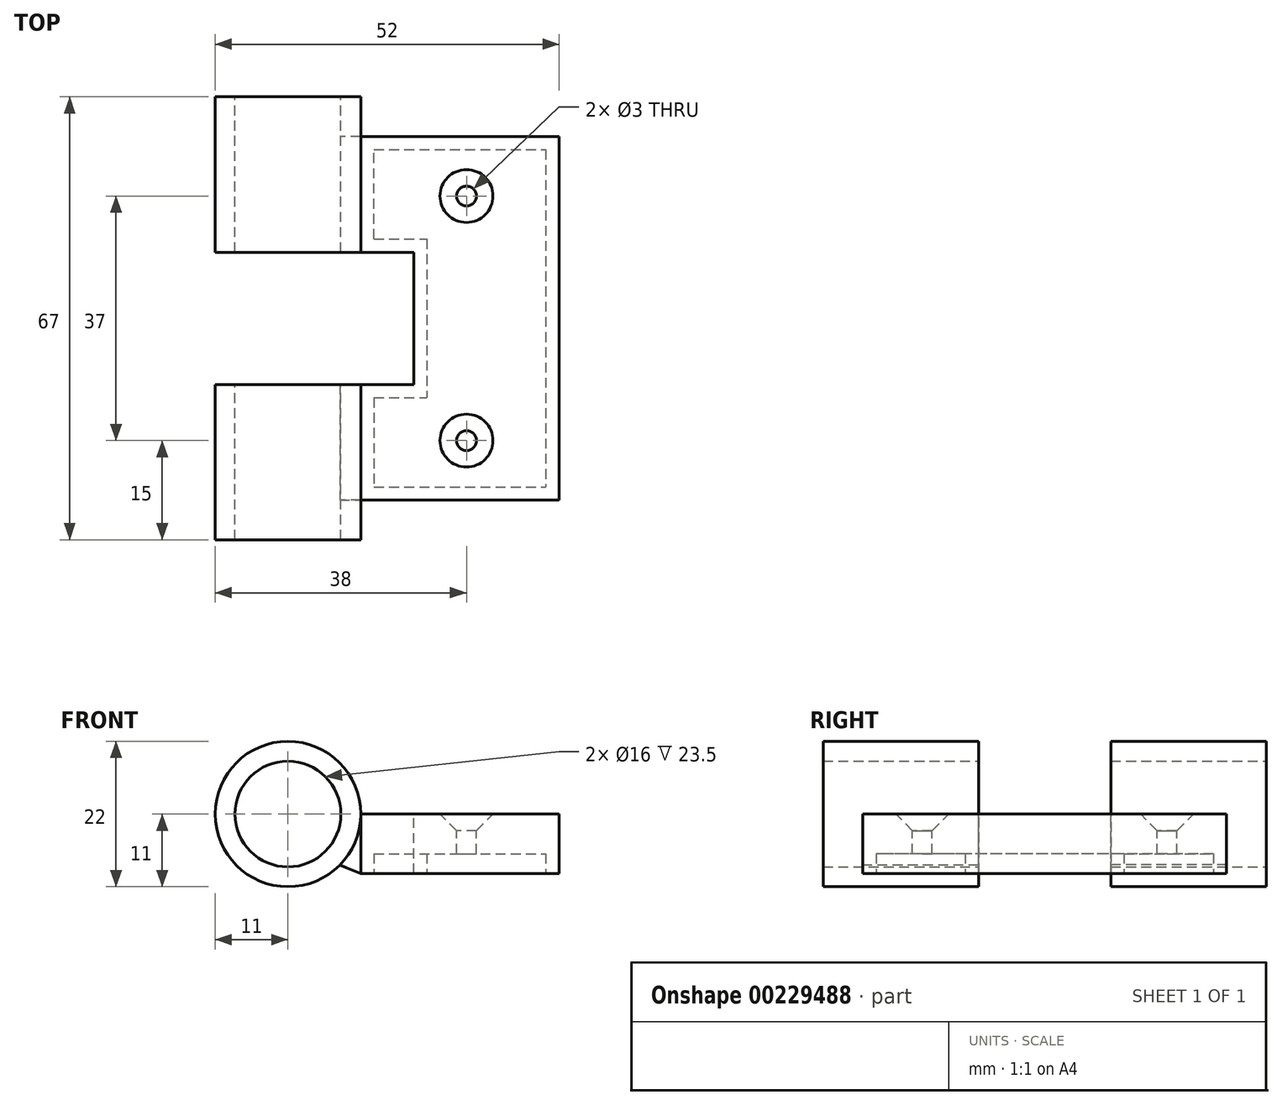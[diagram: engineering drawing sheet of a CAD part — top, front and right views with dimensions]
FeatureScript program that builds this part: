
annotation { "Feature Type Name" : "Feature", "Feature Type Description" : "" }
export const myFeature = defineFeature(function(context is Context, id is Id, definition is map)
    precondition{}
    {
        {
            var Q0;
            Q0=qCreatedBy(makeId("Top.planeOp"),FACE);
            var sketch = newSketch(context, id + "F0", { "sketchPlane" : qUnion([Q0])});
            skLineSegment(sketch, "E0", {"start": v(-15, 0) * mm, "end": v(15, 0) * mm, "construction": true});
            skLineSegment(sketch, "E1.0", {"start": v(-15, -27.5) * mm, "end": v(15, -27.5) * mm});
            skLineSegment(sketch, "E2.0", {"start": v(-15, 27.5) * mm, "end": v(15, 27.5) * mm});
            skLineSegment(sketch, "E3", {"start": v(0, 0) * mm, "end": v(0, 27.5) * mm});
            skLineSegment(sketch, "E4", {"start": v(0, 0) * mm, "end": v(0, -27.5) * mm});
            skLineSegment(sketch, "E5.0", {"start": v(15, 0) * mm, "end": v(15, 27.5) * mm});
            skLineSegment(sketch, "E6.0", {"start": v(-15, -10) * mm, "end": v(-15, -27.5) * mm});
            skLineSegment(sketch, "E7.0", {"start": v(15, 0) * mm, "end": v(15, -27.5) * mm});
            skLineSegment(sketch, "E8.0", {"start": v(-15, 10) * mm, "end": v(-15, 27.5) * mm});
            skPoint(sketch, "E9.orphan", {"position": v(-28.94, 0) * mm});
            skLineSegment(sketch, "E10.0", {"start": v(-15, -10) * mm, "end": v(-7, -10) * mm});
            skLineSegment(sketch, "E11.0", {"start": v(-15, 10) * mm, "end": v(-7, 10) * mm});
            skLineSegment(sketch, "E12.0", {"start": v(-7, 0) * mm, "end": v(-7, 10) * mm});
            skLineSegment(sketch, "E13.0", {"start": v(-7, 0) * mm, "end": v(-7, -10) * mm});
            skSolve(sketch);
        }
        {
            var Q0;
            {var subQ1=sQuery(id+"F0.wireOp",EDGE,"E3");Q0=makeQuery(id+"F0.imprint","IMPRINT",FACE,{"disambiguationData":[TD([[makeQuery(id+"F0.imprint","IMPRINT",EDGE,{"derivedFrom":subQ1}),1.0]])]});}
            var Q1;
            {var subQ1=sQuery(id+"F0.wireOp",EDGE,"E3");Q1=makeQuery(id+"F0.imprint","IMPRINT",FACE,{"disambiguationData":[TD([[makeQuery(id+"F0.imprint","IMPRINT",EDGE,{"derivedFrom":subQ1}),-1.0]])]});}
            extrude(context, id + "F1", {"entities" : qUnion([Q0, Q1]), "oppositeDirection" : true, "depth" : 9 * mm});
        }
        {
            var Q0;
            Q0=makeQuery(id+"F1.opExtrude","CAP_FACE",FACE,{"disambiguationData":[OSD([sQuery(id+"F0.wireOp",EDGE,"E1.0"),sQuery(id+"F0.wireOp",EDGE,"E2.0"),sQuery(id+"F0.wireOp",EDGE,"E5.0"),sQuery(id+"F0.wireOp",EDGE,"E6.0"),sQuery(id+"F0.wireOp",EDGE,"E7.0"),sQuery(id+"F0.wireOp",EDGE,"E8.0"),sQuery(id+"F0.wireOp",EDGE,"E10.0"),sQuery(id+"F0.wireOp",EDGE,"E11.0"),sQuery(id+"F0.wireOp",EDGE,"E12.0"),sQuery(id+"F0.wireOp",EDGE,"E13.0")])],"isStart":false});
            var sketch = newSketch(context, id + "F2", { "sketchPlane" : qUnion([Q0])});
            skLineSegment(sketch, "E14.0", {"start": v(-13, 12) * mm, "end": v(-13, 25.5) * mm});
            skLineSegment(sketch, "E15.0", {"start": v(-13, 25.5) * mm, "end": v(13, 25.5) * mm});
            skLineSegment(sketch, "E16.0", {"start": v(13, -25.5) * mm, "end": v(13, 25.5) * mm});
            skLineSegment(sketch, "E17.0", {"start": v(-13, -25.5) * mm, "end": v(13, -25.5) * mm});
            skLineSegment(sketch, "E18.0", {"start": v(-13, -12) * mm, "end": v(-13, -25.5) * mm});
            skLineSegment(sketch, "E19.0", {"start": v(-13, -12) * mm, "end": v(-7, -12) * mm});
            skLineSegment(sketch, "E20.0", {"start": v(-5, 10) * mm, "end": v(-5, -10) * mm});
            skLineSegment(sketch, "E21.0", {"start": v(-13, 12) * mm, "end": v(-7, 12) * mm});
            skLineSegment(sketch, "E22", {"start": v(-7, 12) * mm, "end": v(-5, 12) * mm});
            skLineSegment(sketch, "E23", {"start": v(-5, 10) * mm, "end": v(-5, 12) * mm});
            skLineSegment(sketch, "E24", {"start": v(-7, -12) * mm, "end": v(-5, -12) * mm});
            skLineSegment(sketch, "E25", {"start": v(-5, -10) * mm, "end": v(-5, -12) * mm});
            skSolve(sketch);
        }
        {
            var Q0;
            Q0=makeQuery(id+"F2.imprint","IMPRINT",FACE,{"disambiguationData":[TD([[makeQuery(id+"F2.imprint","IMPRINT",EDGE,{"derivedFrom":sQuery(id+"F2.wireOp",EDGE,"E14.0")}),-1.0]])]});
            extrude(context, id + "F3", {"entities" : qUnion([Q0]), "operationType" : NewBodyOperationType.REMOVE, "oppositeDirection" : true, "depth" : 3 * mm});
        }
        {
            var Q0;
            Q0=makeQuery(id+"F1.opExtrude","SWEPT_FACE",FACE,{"disambiguationData":[OSD([sQuery(id+"F0.wireOp",EDGE,"E1.0")])]});
            var sketch = newSketch(context, id + "F4", { "sketchPlane" : qUnion([Q0])});
            skCircle(sketch, "E26", {"center": v(-26, 0) * mm, "radius": 11 * mm});
            skCircle(sketch, "E27", {"center": v(-26, 0) * mm, "radius": 8 * mm});
            skLineSegment(sketch, "E28", {"start": v(-15, -9) * mm, "end": v(-18.17, -7.73) * mm});
            skSolve(sketch);
        }
        {
            var Q0;
            Q0=makeQuery(id+"F4.imprint","IMPRINT",FACE,{"disambiguationData":[TD([[makeQuery(id+"F4.imprint","IMPRINT",EDGE,{"derivedFrom":sQuery(id+"F4.wireOp",EDGE,"E27")}),-1.0]])]});
            extrude(context, id + "F5", {"entities" : qUnion([Q0]), "depth" : 6 * mm, "hasSecondDirection" : true, "secondDirectionOppositeDirection" : true, "secondDirectionDepth" : 17.5 * mm});
        }
        {
            var Q0;
            {var subQ3=sQuery(id+"F4.wireOp",EDGE,"E28");Q0=makeQuery(id+"F4.imprint","IMPRINT",FACE,{"disambiguationData":[TD([[makeQuery(id+"F4.imprint","IMPRINT",EDGE,{"derivedFrom":subQ3}),-1.0]])]});}
            extrude(context, id + "F6", {"entities" : qUnion([Q0]), "oppositeDirection" : true, "depth" : 17.5 * mm});
        }
        {
            var Q0;
            Q0=makeQuery(id+"F1.opExtrude","SWEPT_FACE",FACE,{"disambiguationData":[OSD([sQuery(id+"F0.wireOp",EDGE,"E2.0")])]});
            var sketch = newSketch(context, id + "F7", { "sketchPlane" : qUnion([Q0])});
            skCircle(sketch, "E29", {"center": v(26, 0) * mm, "radius": 11 * mm});
            skCircle(sketch, "E30", {"center": v(26, 0) * mm, "radius": 8 * mm});
            skLineSegment(sketch, "E31", {"start": v(15, -9) * mm, "end": v(18.04, -7.59) * mm});
            skSolve(sketch);
        }
        {
            var Q0;
            Q0=makeQuery(id+"F7.imprint","IMPRINT",FACE,{"disambiguationData":[TD([[makeQuery(id+"F7.imprint","IMPRINT",EDGE,{"derivedFrom":sQuery(id+"F7.wireOp",EDGE,"E30")}),-1.0]])]});
            extrude(context, id + "F8", {"entities" : qUnion([Q0]), "oppositeDirection" : true, "depth" : 17.5 * mm, "hasSecondDirection" : true, "secondDirectionOppositeDirection" : false, "secondDirectionDepth" : 6 * mm});
        }
        {
            var Q0;
            {var subQ3=sQuery(id+"F7.wireOp",EDGE,"E31");Q0=makeQuery(id+"F7.imprint","IMPRINT",FACE,{"disambiguationData":[TD([[makeQuery(id+"F7.imprint","IMPRINT",EDGE,{"derivedFrom":subQ3}),1.0]])]});}
            extrude(context, id + "F9", {"entities" : qUnion([Q0]), "operationType" : NewBodyOperationType.ADD, "oppositeDirection" : true, "depth" : 17.5 * mm});
        }
        {
            var Q0;
            Q0=makeQuery(id+"F1.opExtrude","CAP_FACE",FACE,{"disambiguationData":[OSD([sQuery(id+"F0.wireOp",EDGE,"E1.0"),sQuery(id+"F0.wireOp",EDGE,"E2.0"),sQuery(id+"F0.wireOp",EDGE,"E5.0"),sQuery(id+"F0.wireOp",EDGE,"E6.0"),sQuery(id+"F0.wireOp",EDGE,"E7.0"),sQuery(id+"F0.wireOp",EDGE,"E8.0"),sQuery(id+"F0.wireOp",EDGE,"E10.0"),sQuery(id+"F0.wireOp",EDGE,"E11.0"),sQuery(id+"F0.wireOp",EDGE,"E12.0"),sQuery(id+"F0.wireOp",EDGE,"E13.0")])],"isStart":true});
            var sketch = newSketch(context, id + "F10", { "sketchPlane" : qUnion([Q0])});
            skLineSegment(sketch, "E32.0", {"start": v(1, 27.5) * mm, "end": v(1, -27.5) * mm, "construction": true});
            skLineSegment(sketch, "E33.0", {"start": v(-15, 18.5) * mm, "end": v(15, 18.5) * mm, "construction": true});
            skLineSegment(sketch, "E34.0", {"start": v(-15, -18.5) * mm, "end": v(15, -18.5) * mm, "construction": true});
            skPoint(sketch, "E35", {"position": v(1, 18.5) * mm});
            skPoint(sketch, "E36", {"position": v(1, -18.5) * mm});
            skSolve(sketch);
        }
        {
            var Q0;
            Q0=sQuery(id+"F10.wireOp",VERTEX,"E35");
            var Q1;
            Q1=sQuery(id+"F10.wireOp",VERTEX,"E36");
            var Q2;
            Q2=makeQuery(id+"F1.opExtrude","SWEPT_BODY",BODY,{"disambiguationData":[OSD([sQuery(id+"F0.wireOp",EDGE,"E1.0"),sQuery(id+"F0.wireOp",EDGE,"E2.0"),sQuery(id+"F0.wireOp",EDGE,"E5.0"),sQuery(id+"F0.wireOp",EDGE,"E6.0"),sQuery(id+"F0.wireOp",EDGE,"E7.0"),sQuery(id+"F0.wireOp",EDGE,"E8.0"),sQuery(id+"F0.wireOp",EDGE,"E10.0"),sQuery(id+"F0.wireOp",EDGE,"E11.0"),sQuery(id+"F0.wireOp",EDGE,"E12.0"),sQuery(id+"F0.wireOp",EDGE,"E13.0")])]});
            hole(context, id + "F11", {"style" : HoleStyle.C_SINK, "endStyle" : HoleEndStyle.THROUGH, "holeDiameter" : 3 * mm, "cSinkDiameter" : 8 * mm, "cSinkAngle" : 90 * degree, "startFromSketch" : true, "locations" : qUnion([Q0, Q1]), "scope" : qUnion([Q2]), "isTappedThrough" : true});
        }
    });
